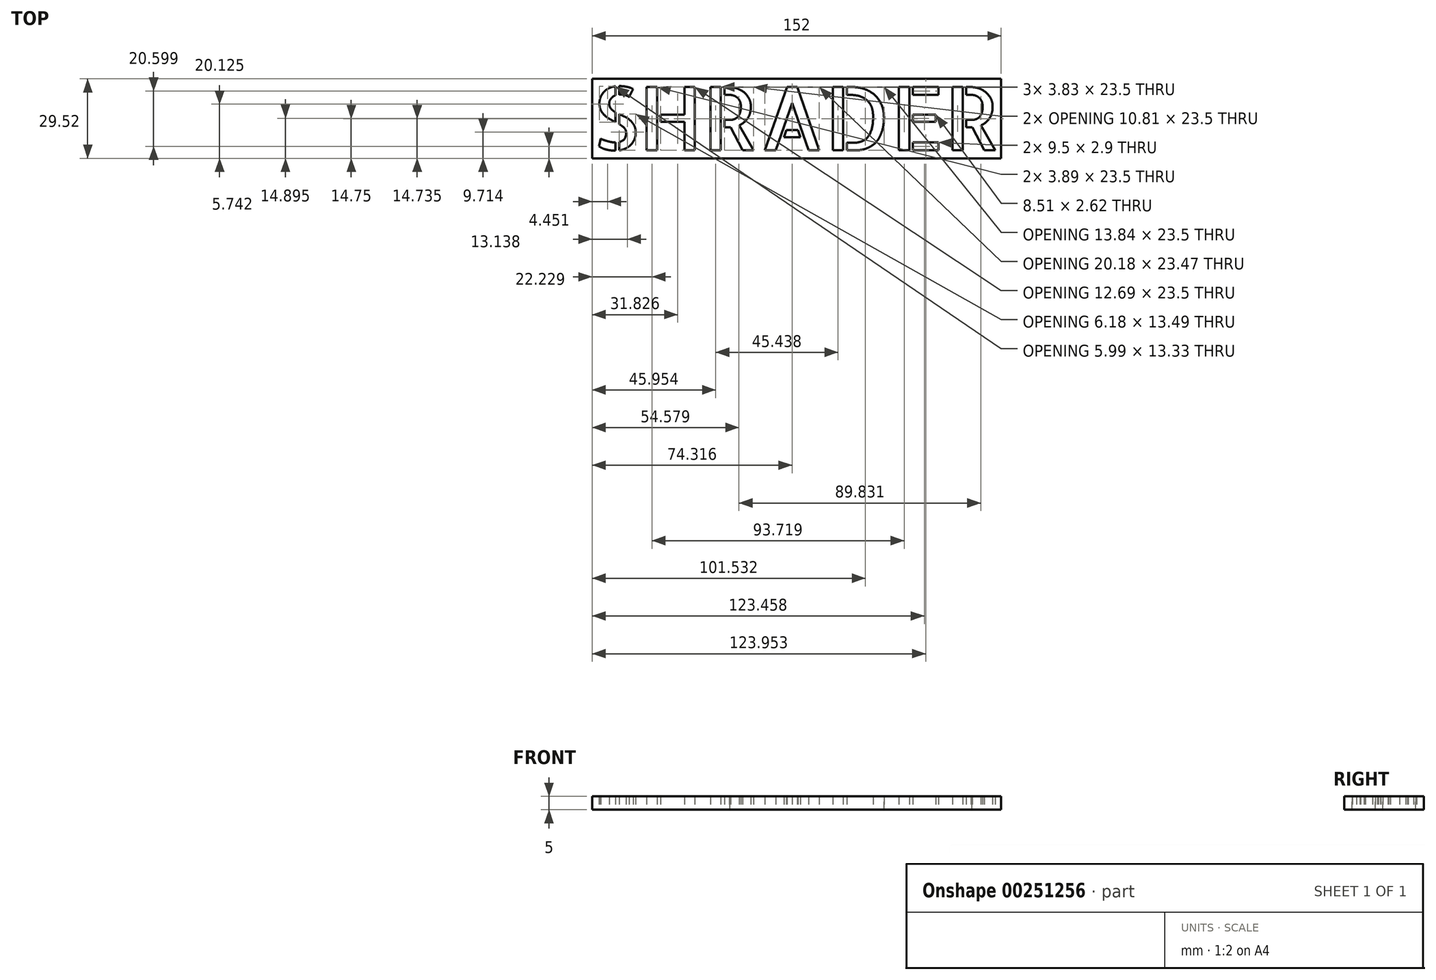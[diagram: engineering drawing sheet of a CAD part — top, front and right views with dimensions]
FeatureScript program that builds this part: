
annotation { "Feature Type Name" : "Feature", "Feature Type Description" : "" }
export const myFeature = defineFeature(function(context is Context, id is Id, definition is map)
    precondition{}
    {
        {
            var Q0;
            Q0=qCreatedBy(makeId("Top.planeOp"),FACE);
            var sketch = newSketch(context, id + "F0", { "sketchPlane" : qUnion([Q0])});
            skText(sketch, "E0", { "text": "SHRADER", "fontName": "AllertaStencil-Regular.ttf"});
            skLineSegment(sketch, "E1.bottom", {"start": v(76, -14.76) * mm, "end": v(-76, -14.76) * mm});
            skLineSegment(sketch, "E1.top", {"start": v(76, 14.76) * mm, "end": v(-76, 14.76) * mm});
            skLineSegment(sketch, "E1.left", {"start": v(76, -14.76) * mm, "end": v(76, 14.76) * mm});
            skLineSegment(sketch, "E1.right", {"start": v(-76, -14.76) * mm, "end": v(-76, 14.76) * mm});
            skPoint(sketch, "E1.middle", {"position": v(0, 0) * mm});
            const initialGuessF0  = {"E0": [-0.076, -0.01176, 1, 0, 0.02351]};
            skSetInitialGuess(sketch, initialGuessF0);
            skSolve(sketch);
        }
        {
            var Q0;
            Q0 = qSketchRegion(id + "F0", true);
            extrude(context, id + "F1", {"entities" : qUnion([Q0]), "depth" : 5 * mm});
        }
    });
